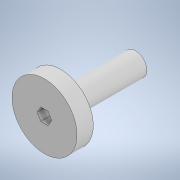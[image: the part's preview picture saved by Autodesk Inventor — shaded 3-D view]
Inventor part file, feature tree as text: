
AUTODESK INVENTOR PART (.ipt)
format: ipt  version: 2022.2 (Build 262287010, 287A)  size: 122,880 bytes
history: native  units: in
note: dims shown in document units (in); Inventor stores cm internally (conversion verified against a paired STEP export)
features: extrude x2, sketch x2
ambient origin geometry x8: Origin, YZ Plane, XZ Plane, XY Plane, X Axis, Y Axis, Z Axis, Center Point
bodies: Solid1 (feature_tree)
feature tree (4):
  extrude  "Extrusion1"  Depth=0.385in
  extrude  "Extrusion2"  Depth=0.5in
  sketch  "Sketch1"  dims[d0=0.385in d1=0.7in]
  sketch  "Sketch2"  dims[d2=2.3in d3=0.0in d4=2.0in d5=0.5in d6=0.0in]
